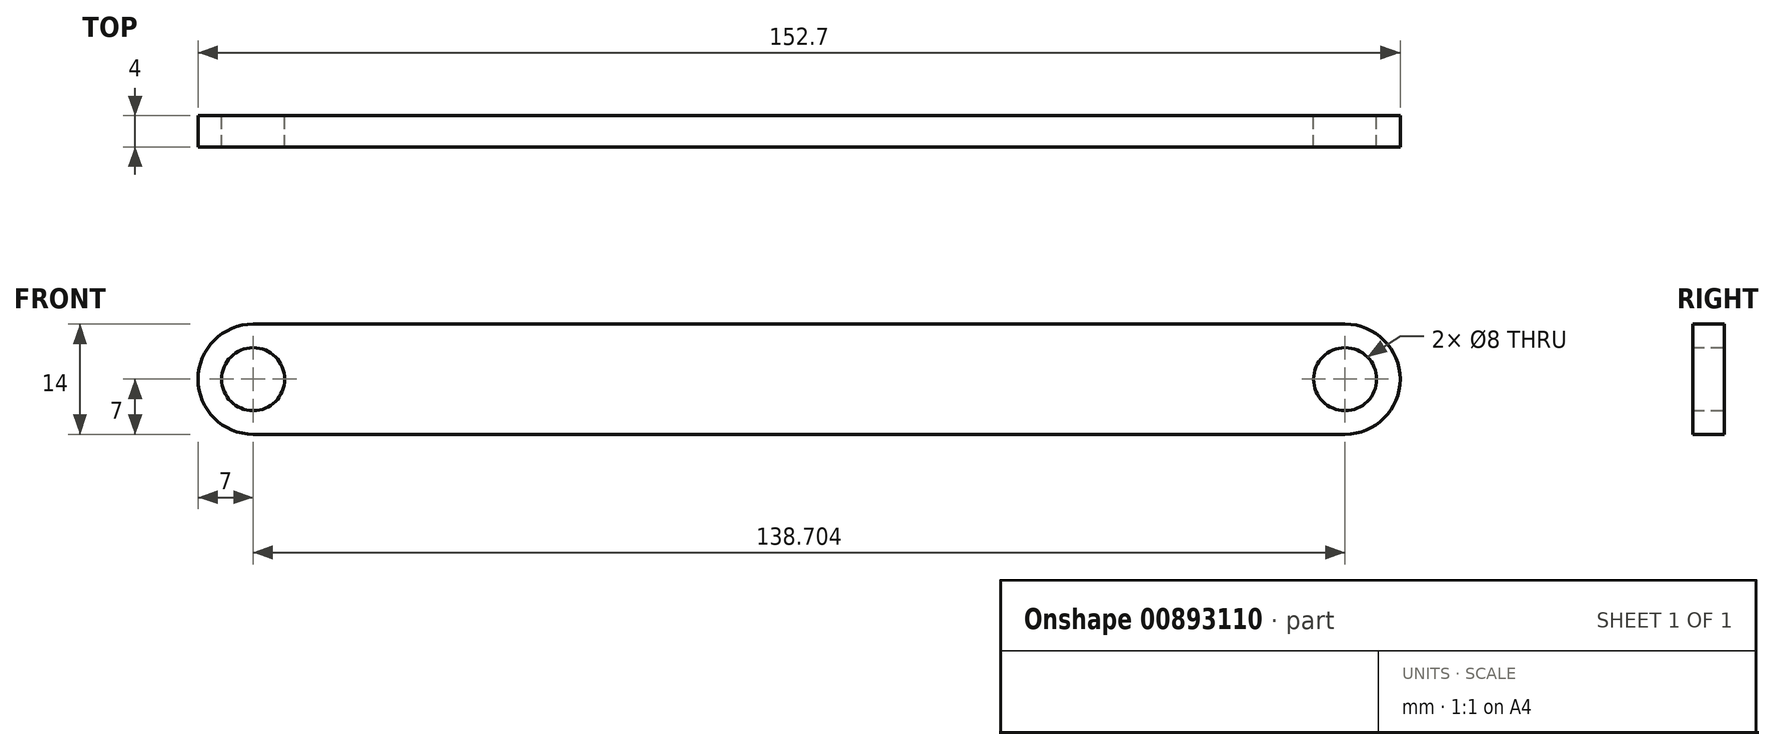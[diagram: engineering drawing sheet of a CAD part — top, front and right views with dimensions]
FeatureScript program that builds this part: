
annotation { "Feature Type Name" : "Feature", "Feature Type Description" : "" }
export const myFeature = defineFeature(function(context is Context, id is Id, definition is map)
    precondition{}
    {
        {
            assignVariable(context, id + "F0", {"name" : "Thickness", "anyValue" : 4});
        }
        {
            var Q0;
            Q0=qCreatedBy(makeId("Front.planeOp"),FACE);
            var sketch = newSketch(context, id + "F1", { "sketchPlane" : qUnion([Q0])});
            skCircle(sketch, "E0", {"center": v(0, 0) * mm, "radius": 4 * mm});
            skCircle(sketch, "E1", {"center": v(138.7, 0) * mm, "radius": 4 * mm});
            skArc(sketch, "E2", {"start": v(138.7, -7) * mm, "mid": v(145.7, 0) * mm, "end": v(138.7, 7) * mm});
            skArc(sketch, "E3", {"start": v(0, 7) * mm, "mid": v(-7, 0) * mm, "end": v(0, -7) * mm});
            skLineSegment(sketch, "E4", {"start": v(0, 7) * mm, "end": v(138.7, 7) * mm});
            skLineSegment(sketch, "E5", {"start": v(0, -7) * mm, "end": v(138.7, -7) * mm});
            skSolve(sketch);
        }
        {
            var Q0;
            Q0=makeQuery(id+"F1.imprint","IMPRINT",FACE,{"disambiguationData":[TD([[makeQuery(id+"F1.imprint","IMPRINT",EDGE,{"derivedFrom":sQuery(id+"F1.wireOp",EDGE,"E0")}),-1.0]])]});
            extrude(context, id + "F2", {"entities" : qUnion([Q0]), "depth" : (getVariable(context, 'Thickness')) * mm, "offsetDistance" : 25 * mm});
        }
    });
